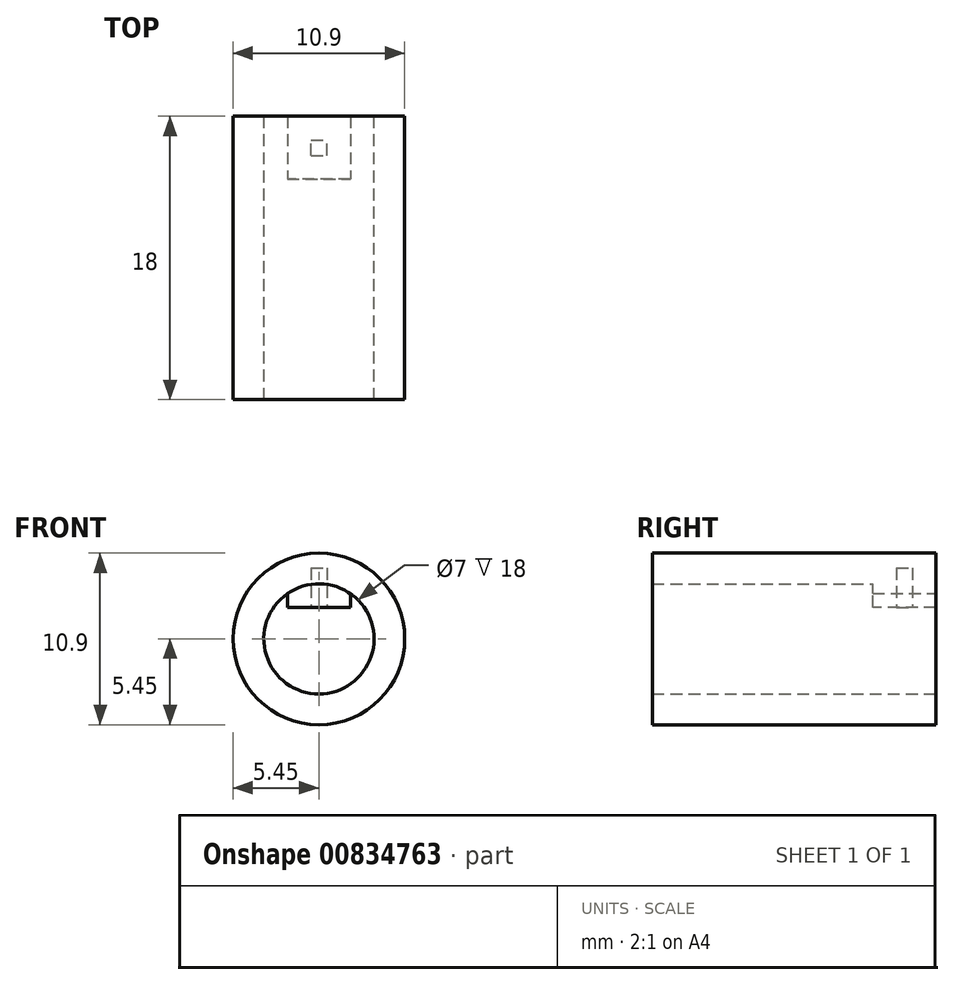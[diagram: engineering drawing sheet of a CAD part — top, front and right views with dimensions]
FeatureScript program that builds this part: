
annotation { "Feature Type Name" : "Feature", "Feature Type Description" : "" }
export const myFeature = defineFeature(function(context is Context, id is Id, definition is map)
    precondition{}
    {
        {
            var Q0;
            Q0=qCreatedBy(makeId("Front.planeOp"),FACE);
            var sketch = newSketch(context, id + "F0", { "sketchPlane" : qUnion([Q0])});
            skCircle(sketch, "E0", {"center": v(0, 0) * mm, "radius": 5.45 * mm});
            skCircle(sketch, "E1", {"center": v(0, 0) * mm, "radius": 3.5 * mm});
            skLineSegment(sketch, "E2", {"start": v(2, 3.5) * mm, "end": v(-2, 3.5) * mm});
            skLineSegment(sketch, "E3", {"start": v(0, 3.5) * mm, "end": v(0, 3.83) * mm});
            skSolve(sketch);
        }
        {
            var Q0;
            Q0=makeQuery(id+"F0.imprint","IMPRINT",FACE,{"disambiguationData":[TD([[makeQuery(id+"F0.imprint","IMPRINT",EDGE,{"derivedFrom":sQuery(id+"F0.wireOp",EDGE,"E0")}),1.0]])]});
            extrude(context, id + "F1", {"entities" : qUnion([Q0]), "depth" : 18 * mm, "offsetDistance" : 25 * mm});
        }
        {
            var Q0;
            Q0=sQuery(id+"F0.wireOp",EDGE,"E2");
            extrude(context, id + "F2", {"bodyType" : ToolBodyType.SURFACE, "operationType" : NewBodyOperationType.INTERSECT, "surfaceEntities" : qUnion([Q0]), "depth" : 4 * mm, "offsetDistance" : 25 * mm});
        }
        {
            var Q0;
            Q0=makeQuery(id+"F2.opExtrude","SWEPT_FACE",FACE,{"disambiguationData":[OSD([sQuery(id+"F0.wireOp",EDGE,"E2")])]});
            extrude(context, id + "F3", {"entities" : qUnion([Q0]), "operationType" : NewBodyOperationType.ADD, "oppositeDirection" : true, "depth" : 1.5 * mm, "offsetDistance" : 25 * mm});
        }
        {
            var Q0;
            Q0=makeQuery(id+"F3.opExtrude","CAP_FACE",FACE,{"disambiguationData":[OSD([sQuery(id+"F0.wireOp",EDGE,"E2")])],"isStart":false});
            var sketch = newSketch(context, id + "F4", { "sketchPlane" : qUnion([Q0])});
            skLineSegment(sketch, "E4.bottom", {"start": v(-0.5, 2.5) * mm, "end": v(0.5, 2.5) * mm});
            skLineSegment(sketch, "E4.top", {"start": v(-0.5, 1.5) * mm, "end": v(0.5, 1.5) * mm});
            skLineSegment(sketch, "E4.left", {"start": v(-0.5, 2.5) * mm, "end": v(-0.5, 1.5) * mm});
            skLineSegment(sketch, "E4.right", {"start": v(0.5, 2.5) * mm, "end": v(0.5, 1.5) * mm});
            skPoint(sketch, "E4.middle", {"position": v(0, 2) * mm});
            skSolve(sketch);
        }
        {
            var Q0;
            Q0=makeQuery(id+"F4.imprint","IMPRINT",FACE,{"disambiguationData":[TD([[makeQuery(id+"F4.imprint","IMPRINT",EDGE,{"derivedFrom":sQuery(id+"F4.wireOp",EDGE,"E4.bottom")}),-1.0]])]});
            extrude(context, id + "F5", {"entities" : qUnion([Q0]), "operationType" : NewBodyOperationType.REMOVE, "oppositeDirection" : true, "depth" : 2.5 * mm, "offsetDistance" : 25 * mm});
        }
    });
